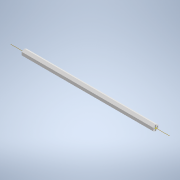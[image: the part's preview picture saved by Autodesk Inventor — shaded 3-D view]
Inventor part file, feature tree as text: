
AUTODESK INVENTOR PART (.ipt)
format: ipt  version: 2020.2 (Build 242310000, 310)  size: 98,304 bytes
history: native  units: in
note: dims shown in document units (in); Inventor stores cm internally (conversion verified against a paired STEP export)
features: sketch x3, extrude x1, other x1
ambient origin geometry x8: Origin, YZ Plane, XZ Plane, XY Plane, X Axis, Y Axis, Z Axis, Center Point
bodies: Solid1 (feature_tree)
feature tree (5):
  extrude  "Extrusion1"  [1 undecoded]
  sketch  "Sketch2"
  sketch  "Sketch3"
  other  "Work Axis1"
  sketch  "Sketch1"  dims[d0=5.3125in d1=0.0in]
note: 1 required parameter value undecoded (feature->parameter linkage not recoverable at this tier; creation-order binding heuristic only, values carry confidence <= 0.55)
